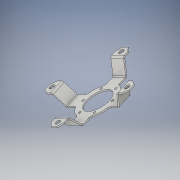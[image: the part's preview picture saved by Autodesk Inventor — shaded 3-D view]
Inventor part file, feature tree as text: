
AUTODESK INVENTOR PART (.ipt)
format: ipt  version: 2019 (Build 230136000, 136)  size: 709,632 bytes
history: native  units: mm
features: sheet_metal_op x9, other x9, sketch x9, chamfer x1
ambient origin geometry x8: Origin, YZ Plane, XZ Plane, XY Plane, X Axis, Y Axis, Z Axis, Center Point
bodies: Solid1 (feature_tree)
feature tree (28):
  sheet_metal_op  "Face1"
  chamfer  "Corner Round1"
  sheet_metal_op  "Fold1"
  sheet_metal_op  "Fold2"
  sheet_metal_op  "Fold3"
  sheet_metal_op  "Fold4"
  sheet_metal_op  "Fold5"
  sheet_metal_op  "Fold6"
  sheet_metal_op  "Fold7"
  sheet_metal_op  "Fold8"
  other  "Corner Chamfer1"
  other  "Corner Chamfer2"
  other  "Corner Chamfer3"
  other  "Corner Chamfer4"
  other  "Corner Chamfer5"
  other  "Corner Chamfer6"
  other  "Corner Chamfer7"
  other  "Corner Chamfer8"
  sketch  "Sketch1"  dims[d0=20.0mm]
  other  "Plate1"
  sketch  "Sketch2"  dims[d1=30.0mm]
  sketch  "Sketch3"  dims[d2=25.0mm]
  sketch  "Sketch4"  dims[d3=2.0mm]
  sketch  "Sketch5"  dims[d4=60.0mm d6=360.0deg]
  sketch  "Sketch7"  dims[d8=30.0mm]
  sketch  "Sketch8"  dims[d9=40.0mm d11=360.0deg]
  sketch  "Sketch9"  dims[d13=4.0mm]
  sketch  "Sketch10"  dims[d14=5.38mm d15=4.0mm d16=5.38mm d17=40.0mm d19=360.0deg d21=1.0mm d22=2.0mm d23=45.0mm d24=1.0mm d25=0.5mm d26=2.0mm d27=1.0mm d28=60.0deg d29=1.0mm d30=45.0mm d31=1.0mm d32=0.5mm d33=2.0mm d34=1.0mm d35=60.0deg d36=1.0mm d37=45.0mm d38=1.0mm d39=0.5mm d40=2.0mm d41=1.0mm d42=60.0deg d43=1.0mm d44=45.0mm d45=1.0mm d46=0.5mm d47=2.0mm d48=1.0mm d49=60.0deg d50=1.0mm d51=8.0mm d52=1.0mm d53=0.5mm d54=2.0mm d55=1.0mm d56=60.0deg d57=1.0mm d58=8.0mm d59=1.0mm d60=0.5mm d61=2.0mm d62=1.0mm d63=60.0deg d64=1.0mm d65=8.0mm d66=1.0mm d67=0.5mm d68=2.0mm d69=1.0mm d70=60.0deg d71=1.0mm d72=8.0mm d73=1.0mm d74=0.5mm d75=2.0mm d76=1.0mm d77=60.0deg d78=1.0mm d79=4.0mm d80=3.0mm d81=45.0deg d82=4.0mm d83=3.0mm d84=45.0deg d85=4.0mm d86=3.0mm d87=45.0deg d88=4.0mm d89=3.0mm d90=45.0deg d91=3.0mm d92=4.0mm d93=45.0deg d94=3.0mm d95=4.0mm d96=45.0deg d97=3.0mm d98=4.0mm d99=45.0deg d100=3.0mm d101=4.0mm d102=45.0deg]
